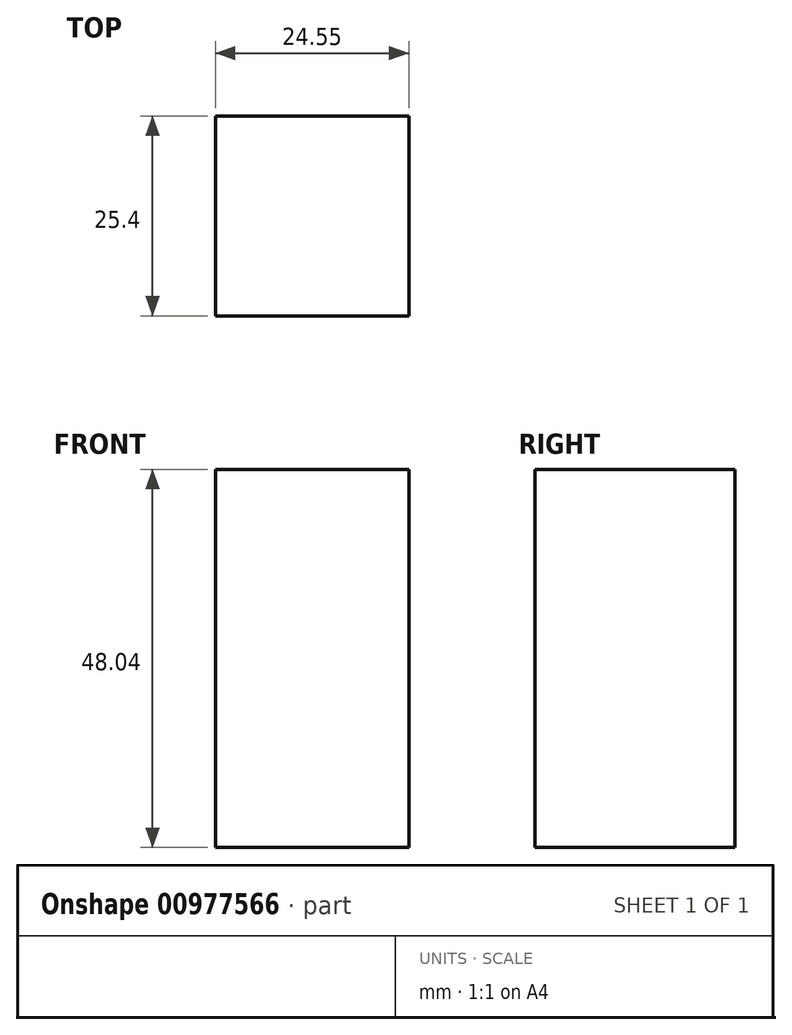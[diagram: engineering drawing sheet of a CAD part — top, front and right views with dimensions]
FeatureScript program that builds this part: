
annotation { "Feature Type Name" : "Feature", "Feature Type Description" : "" }
export const myFeature = defineFeature(function(context is Context, id is Id, definition is map)
    precondition{}
    {
        {
            var Q0;
            Q0=qCreatedBy(makeId("Front.planeOp"),FACE);
            var sketch = newSketch(context, id + "F0", { "sketchPlane" : qUnion([Q0])});
            skLineSegment(sketch, "E0.bottom", {"start": v(0, 0) * mm, "end": v(-24.55, 0) * mm});
            skLineSegment(sketch, "E0.top", {"start": v(0, 48.04) * mm, "end": v(-24.55, 48.04) * mm});
            skLineSegment(sketch, "E0.left", {"start": v(0, 0) * mm, "end": v(0, 48.04) * mm});
            skLineSegment(sketch, "E0.right", {"start": v(-24.55, 0) * mm, "end": v(-24.55, 48.04) * mm});
            skSolve(sketch);
        }
        {
            var Q0;
            Q0=makeQuery(id+"F0.imprint","IMPRINT",FACE,{"disambiguationData":[TD([[makeQuery(id+"F0.imprint","IMPRINT",EDGE,{"derivedFrom":sQuery(id+"F0.wireOp",EDGE,"E0.bottom")}),-1.0]])]});
            extrude(context, id + "F1", {"entities" : qUnion([Q0]), "depth" : 25.4 * mm, "offsetDistance" : 25.4 * mm});
        }
    });
